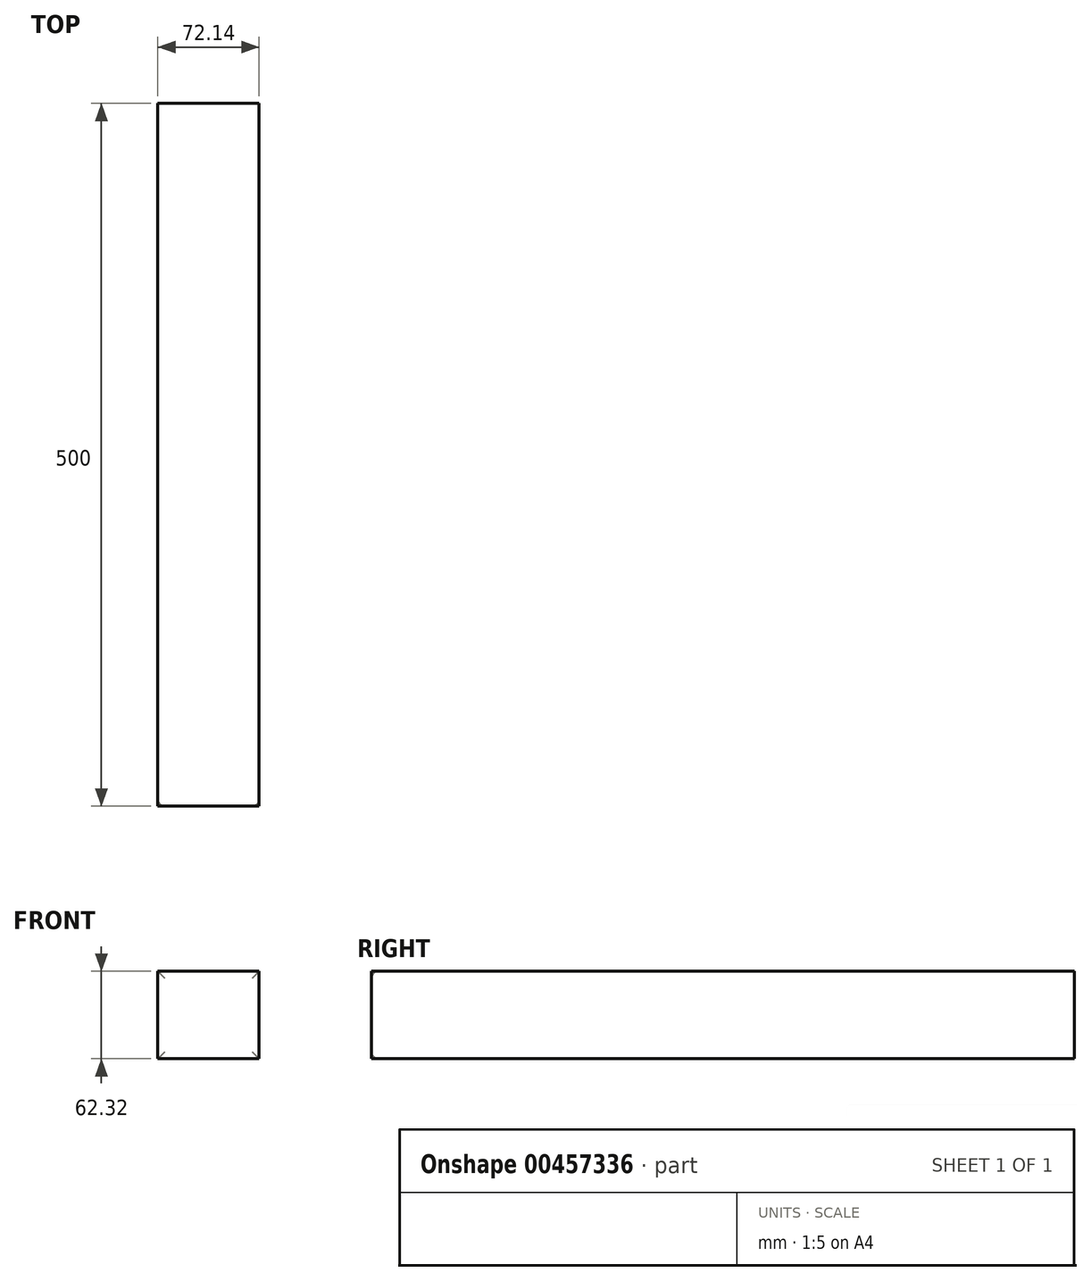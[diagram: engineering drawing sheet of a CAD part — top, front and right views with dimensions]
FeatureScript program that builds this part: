
annotation { "Feature Type Name" : "Feature", "Feature Type Description" : "" }
export const myFeature = defineFeature(function(context is Context, id is Id, definition is map)
    precondition{}
    {
        {
            var Q0;
            Q0=qCreatedBy(makeId("Front.planeOp"),FACE);
            var sketch = newSketch(context, id + "F0", { "sketchPlane" : qUnion([Q0])});
            skLineSegment(sketch, "E0.bottom", {"start": v(0, 63.03) * mm, "end": v(72.14, 63.03) * mm});
            skLineSegment(sketch, "E0.top", {"start": v(0, 0.7) * mm, "end": v(72.14, 0.7) * mm});
            skLineSegment(sketch, "E0.left", {"start": v(72.14, 63.03) * mm, "end": v(72.14, 0.7) * mm});
            skLineSegment(sketch, "E0.right", {"start": v(0, 63.03) * mm, "end": v(0, 0.7) * mm});
            skSolve(sketch);
        }
        {
            var Q0;
            Q0 = qSketchRegion(id + "F0", true);
            var sketch = newSketch(context, id + "F1", { "sketchPlane" : qUnion([Q0])});
            skSolve(sketch);
        }
        {
            var Q0;
            Q0=makeQuery(id+"F0.imprint","IMPRINT",FACE,{"disambiguationData":[TD([[makeQuery(id+"F0.imprint","IMPRINT",EDGE,{"derivedFrom":sQuery(id+"F0.wireOp",EDGE,"E0.bottom")}),-1.0]])]});
            var Q1;
            Q1=makeQuery(id+"F1.imprint","IMPRINT",FACE,{"disambiguationData":[TD([[makeQuery(id+"F1.imprint","IMPRINT",EDGE,{"derivedFrom":makeQuery(id+"F0.imprint","IMPRINT",EDGE,{"derivedFrom":sQuery(id+"F0.wireOp",EDGE,"E0.bottom")})}),-1.0]])]});
            extrude(context, id + "F2", {"entities" : qUnion([Q0, Q1]), "endBound" : BoundingType.SYMMETRIC, "depth" : 500 * mm});
        }
        {
            var Q0;
            {var subQ0=sQuery(id+"F0.wireOp",EDGE,"E0.right");var subQ1=sQuery(id+"F0.wireOp",EDGE,"E0.left");var subQ2=sQuery(id+"F0.wireOp",EDGE,"E0.top");var subQ3=sQuery(id+"F0.wireOp",EDGE,"E0.bottom");Q0=makeQuery(id+"F2.opExtrude","CAP_FACE",FACE,{"disambiguationData":[OSD([subQ3,subQ2,subQ1,subQ0]),TDD([makeQuery(id+"F1.imprint","IMPRINT",EDGE,{"derivedFrom":makeQuery(id+"F0.imprint","IMPRINT",EDGE,{"derivedFrom":subQ3})}),makeQuery(id+"F1.imprint","IMPRINT",EDGE,{"derivedFrom":makeQuery(id+"F0.imprint","IMPRINT",EDGE,{"derivedFrom":subQ2})}),makeQuery(id+"F1.imprint","IMPRINT",EDGE,{"derivedFrom":makeQuery(id+"F0.imprint","IMPRINT",EDGE,{"derivedFrom":subQ1})}),makeQuery(id+"F1.imprint","IMPRINT",EDGE,{"derivedFrom":makeQuery(id+"F0.imprint","IMPRINT",EDGE,{"derivedFrom":subQ0})})])],"isStart":false});}
            fillet(context, id + "F3", {"entities" : qUnion([Q0]), "radius" : 5 * mm, "tangentPropagation" : true, "allowEdgeOverflow" : false});
        }
    });
